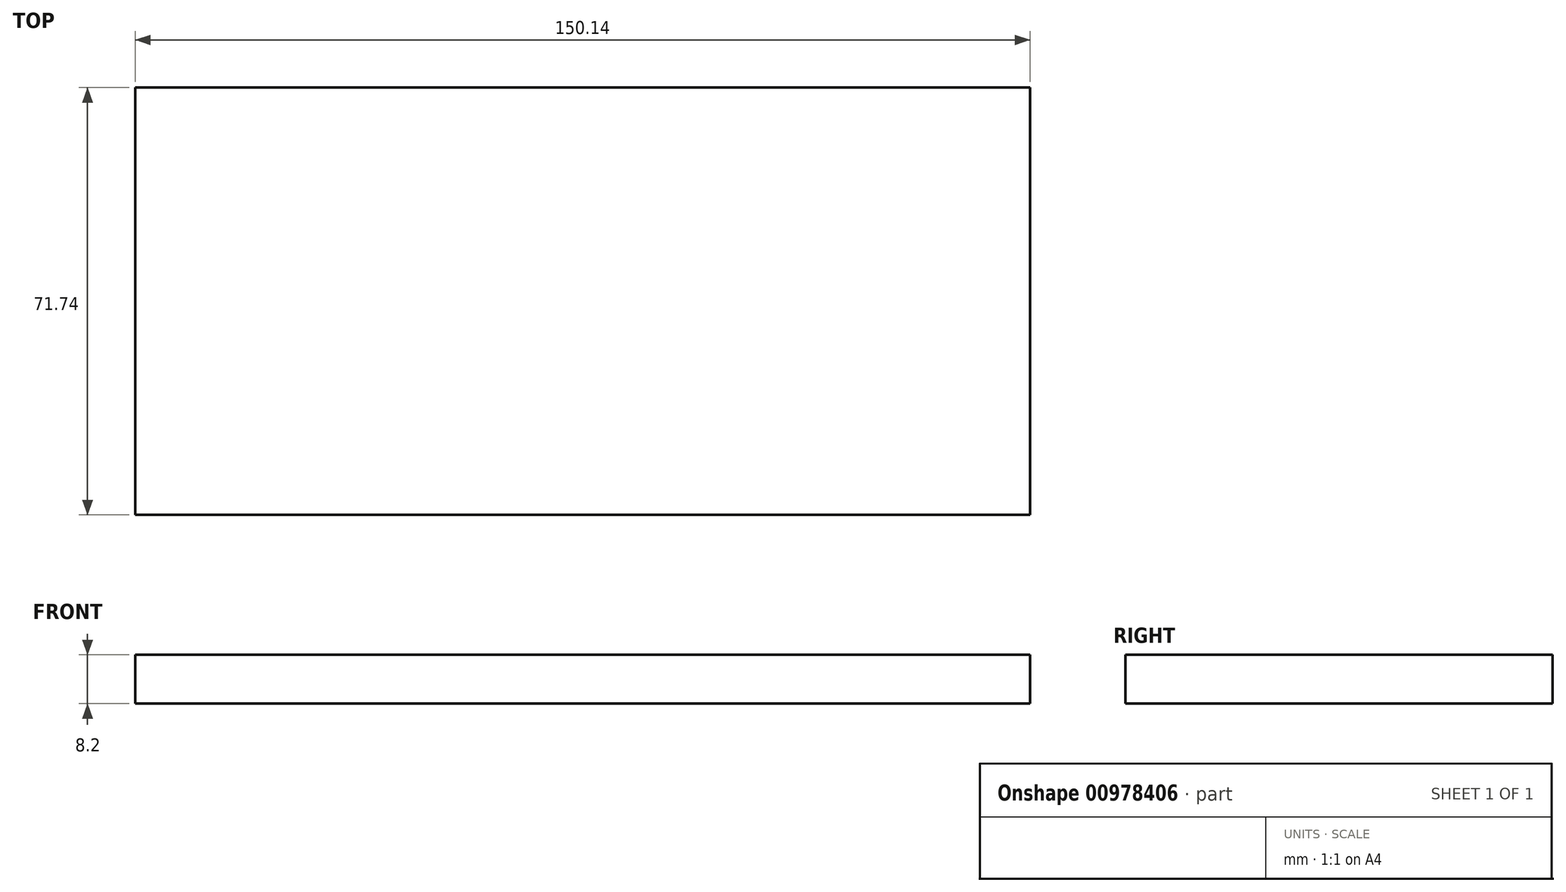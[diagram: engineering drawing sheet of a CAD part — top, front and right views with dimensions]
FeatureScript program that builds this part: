
annotation { "Feature Type Name" : "Feature", "Feature Type Description" : "" }
export const myFeature = defineFeature(function(context is Context, id is Id, definition is map)
    precondition{}
    {
        {
            var Q0;
            Q0=qCreatedBy(makeId("Top.planeOp"),FACE);
            var sketch = newSketch(context, id + "F0", { "sketchPlane" : qUnion([Q0])});
            skLineSegment(sketch, "E0.bottom", {"start": v(-74.84, 34.72) * mm, "end": v(75.3, 34.72) * mm});
            skLineSegment(sketch, "E0.top", {"start": v(-74.84, -37.02) * mm, "end": v(75.3, -37.02) * mm});
            skLineSegment(sketch, "E0.left", {"start": v(-74.84, 34.72) * mm, "end": v(-74.84, -37.02) * mm});
            skLineSegment(sketch, "E0.right", {"start": v(75.3, 34.72) * mm, "end": v(75.3, -37.02) * mm});
            skSolve(sketch);
        }
        {
            var Q0;
            Q0=makeQuery(id+"F0.imprint","IMPRINT",FACE,{"disambiguationData":[TD([[makeQuery(id+"F0.imprint","IMPRINT",EDGE,{"derivedFrom":sQuery(id+"F0.wireOp",EDGE,"E0.bottom")}),-1.0]])]});
            extrude(context, id + "F1", {"entities" : qUnion([Q0]), "depth" : 8.2 * mm, "offsetDistance" : 25 * mm});
        }
    });
